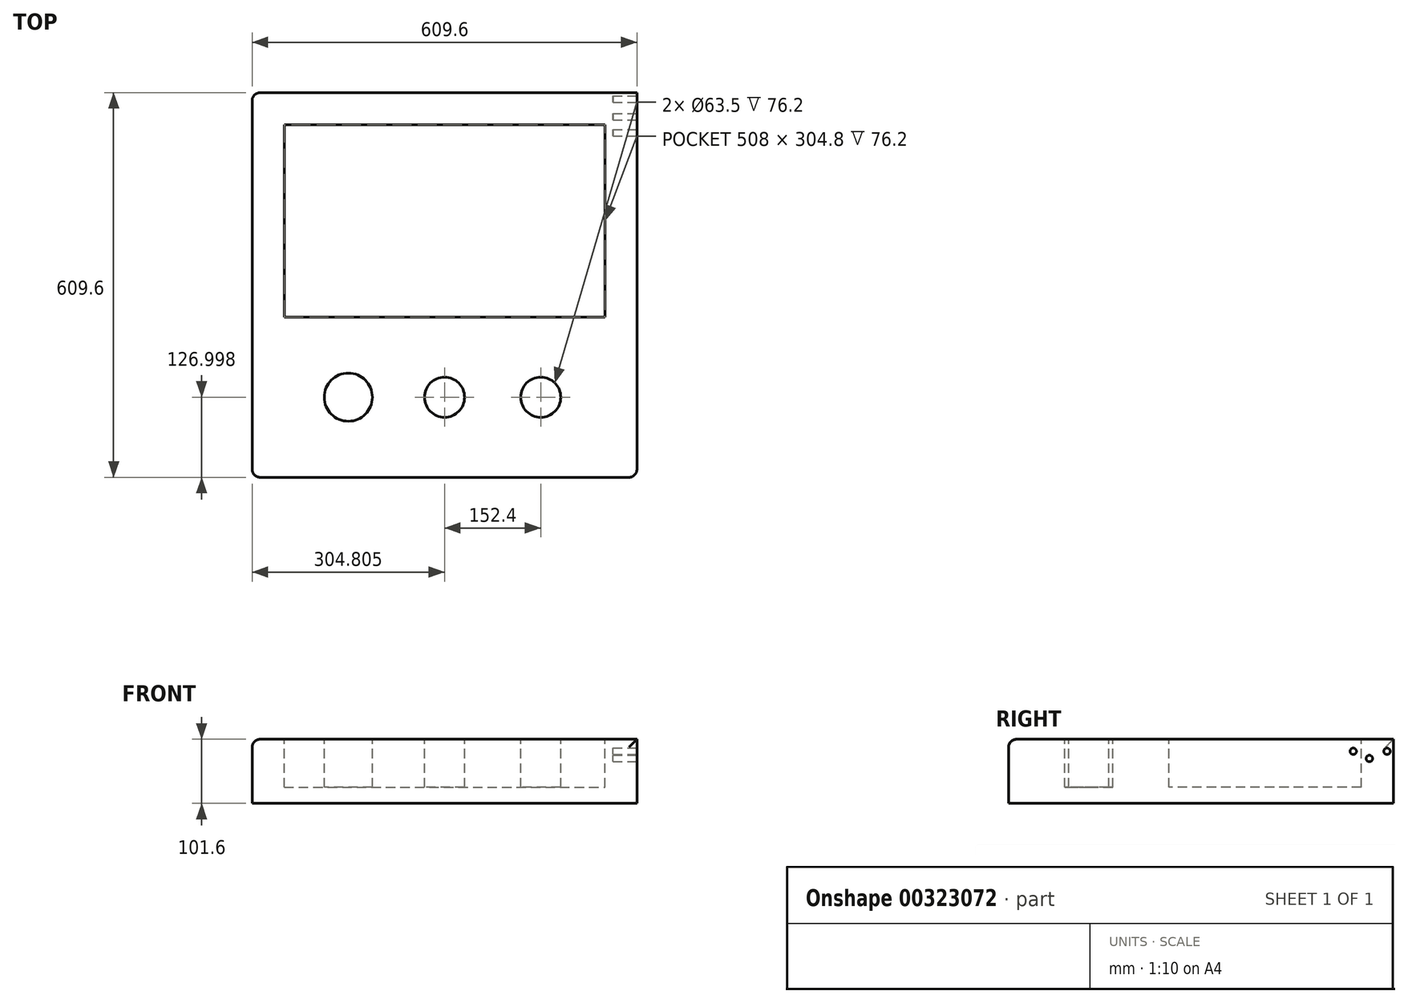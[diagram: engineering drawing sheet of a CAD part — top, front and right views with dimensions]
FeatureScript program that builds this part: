
annotation { "Feature Type Name" : "Feature", "Feature Type Description" : "" }
export const myFeature = defineFeature(function(context is Context, id is Id, definition is map)
    precondition{}
    {
        {
            var Q0;
            Q0=qCreatedBy(makeId("Top.planeOp"),FACE);
            var sketch = newSketch(context, id + "F0", { "sketchPlane" : qUnion([Q0])});
            skLineSegment(sketch, "E0.bottom", {"start": v(-342.87, 305.96) * mm, "end": v(266.73, 305.96) * mm});
            skLineSegment(sketch, "E0.top", {"start": v(-342.87, -303.64) * mm, "end": v(266.73, -303.64) * mm});
            skLineSegment(sketch, "E0.left", {"start": v(-342.87, 305.96) * mm, "end": v(-342.87, -303.64) * mm});
            skLineSegment(sketch, "E0.right", {"start": v(266.73, 305.96) * mm, "end": v(266.73, -303.64) * mm});
            skSolve(sketch);
        }
        {
            var Q0;
            Q0=makeQuery(id+"F0.imprint","IMPRINT",FACE,{"disambiguationData":[TD([[makeQuery(id+"F0.imprint","IMPRINT",EDGE,{"derivedFrom":sQuery(id+"F0.wireOp",EDGE,"E0.bottom")}),-1.0]])]});
            extrude(context, id + "F1", {"entities" : qUnion([Q0]), "depth" : 101.6 * mm});
        }
        {
            var Q0;
            Q0=makeQuery(id+"F1.opExtrude","CAP_FACE",FACE,{"disambiguationData":[OSD([sQuery(id+"F0.wireOp",EDGE,"E0.bottom"),sQuery(id+"F0.wireOp",EDGE,"E0.top"),sQuery(id+"F0.wireOp",EDGE,"E0.left"),sQuery(id+"F0.wireOp",EDGE,"E0.right")])],"isStart":false});
            var sketch = newSketch(context, id + "F2", { "sketchPlane" : qUnion([Q0])});
            skLineSegment(sketch, "E1.bottom", {"start": v(-292.07, 255.16) * mm, "end": v(215.93, 255.16) * mm});
            skLineSegment(sketch, "E1.top", {"start": v(-292.07, -49.64) * mm, "end": v(215.93, -49.64) * mm});
            skLineSegment(sketch, "E1.left", {"start": v(-292.07, 255.16) * mm, "end": v(-292.07, -49.64) * mm});
            skLineSegment(sketch, "E1.right", {"start": v(215.93, 255.16) * mm, "end": v(215.93, -49.64) * mm});
            skCircle(sketch, "E2", {"center": v(-190.47, -176.64) * mm, "radius": 38.1 * mm});
            skCircle(sketch, "E3", {"center": v(-38.07, -176.64) * mm, "radius": 31.75 * mm});
            skCircle(sketch, "E4", {"center": v(114.33, -176.64) * mm, "radius": 31.75 * mm});
            skSolve(sketch);
        }
        {
            var Q0;
            Q0 = qSketchRegion(id + "F2", true);
            extrude(context, id + "F3", {"entities" : qUnion([Q0]), "operationType" : NewBodyOperationType.REMOVE, "oppositeDirection" : true, "depth" : 76.2 * mm});
        }
        {
            var Q0;
            Q0=makeQuery(id+"F1.opExtrude","CAP_EDGE",EDGE,{"disambiguationData":[OSD([sQuery(id+"F0.wireOp",EDGE,"E0.top")])],"isStart":false});
            var Q1;
            Q1=makeQuery(id+"F1.opExtrude","SWEPT_EDGE",EDGE,{"disambiguationData":[OSD([sQuery(id+"F0.wireOp",EDGE,"E0.top"),sQuery(id+"F0.wireOp",EDGE,"E0.right")])]});
            var Q2;
            Q2=makeQuery(id+"F1.opExtrude","CAP_EDGE",EDGE,{"disambiguationData":[OSD([sQuery(id+"F0.wireOp",EDGE,"E0.left")])],"isStart":false});
            var Q3;
            Q3=makeQuery(id+"F1.opExtrude","SWEPT_EDGE",EDGE,{"disambiguationData":[OSD([sQuery(id+"F0.wireOp",EDGE,"E0.top"),sQuery(id+"F0.wireOp",EDGE,"E0.left")])]});
            var Q4;
            Q4=makeQuery(id+"F1.opExtrude","SWEPT_EDGE",EDGE,{"disambiguationData":[OSD([sQuery(id+"F0.wireOp",EDGE,"E0.bottom"),sQuery(id+"F0.wireOp",EDGE,"E0.left")])]});
            fillet(context, id + "F4", {"entities" : qUnion([Q0, Q1, Q2, Q3, Q4]), "radius" : 12.7 * mm, "tangentPropagation" : true, "allowEdgeOverflow" : false});
        }
        {
            var Q0;
            Q0=makeQuery(id+"F1.opExtrude","SWEPT_FACE",FACE,{"disambiguationData":[OSD([sQuery(id+"F0.wireOp",EDGE,"E0.right")])]});
            var sketch = newSketch(context, id + "F5", { "sketchPlane" : qUnion([Q0])});
            skCircle(sketch, "E5", {"center": v(242.36, 82.55) * mm, "radius": 5.08 * mm});
            skCircle(sketch, "E6", {"center": v(267.86, 71.12) * mm, "radius": 5.08 * mm});
            skCircle(sketch, "E7", {"center": v(295.8, 82.55) * mm, "radius": 5.08 * mm});
            skSolve(sketch);
        }
        {
            var Q0;
            Q0 = qSketchRegion(id + "F5", true);
            extrude(context, id + "F6", {"entities" : qUnion([Q0]), "operationType" : NewBodyOperationType.REMOVE, "oppositeDirection" : true, "depth" : 38.1 * mm});
        }
    });
